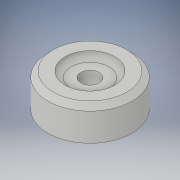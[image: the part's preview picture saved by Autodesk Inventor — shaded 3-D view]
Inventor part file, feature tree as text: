
AUTODESK INVENTOR PART (.ipt)
format: ipt  version: 2018 (Build 220112000, 112)  size: 148,992 bytes
history: native  units: in
note: dims shown in document units (in); Inventor stores cm internally (conversion verified against a paired STEP export)
features: sketch x3, revolve x2, extrude x1, chamfer x1
ambient origin geometry x8: Origin, YZ Plane, XZ Plane, XY Plane, X Axis, Y Axis, Z Axis, Center Point
bodies: Solid1 (feature_tree)
feature tree (7):
  revolve  "Revolution1"  Angle=45.0deg
  revolve  "Revolution3"  [1 undecoded]
  extrude  "Extrusion4"  TaperAngle=90.0deg  [1 undecoded]
  chamfer  "Chamfer3"  Distance=0.115in
  sketch  "Sketch1"  dims[d0=0.125in d5=45.0deg]
  sketch  "Sketch8"  dims[d6=0.0625in d7=0.125in]
  sketch  "Sketch9"  dims[d8=0.25in d9=90.0deg d14=0.115in d31=0.139in d32=0.1562in d33=90.0deg d34=0.2188in d35=0.0695in d36=0.0in d37=0.5in d38=0.0625in d39=0.125in d40=45.0deg]
note: 2 required parameter values undecoded (feature->parameter linkage not recoverable at this tier; creation-order binding heuristic only, values carry confidence <= 0.55)